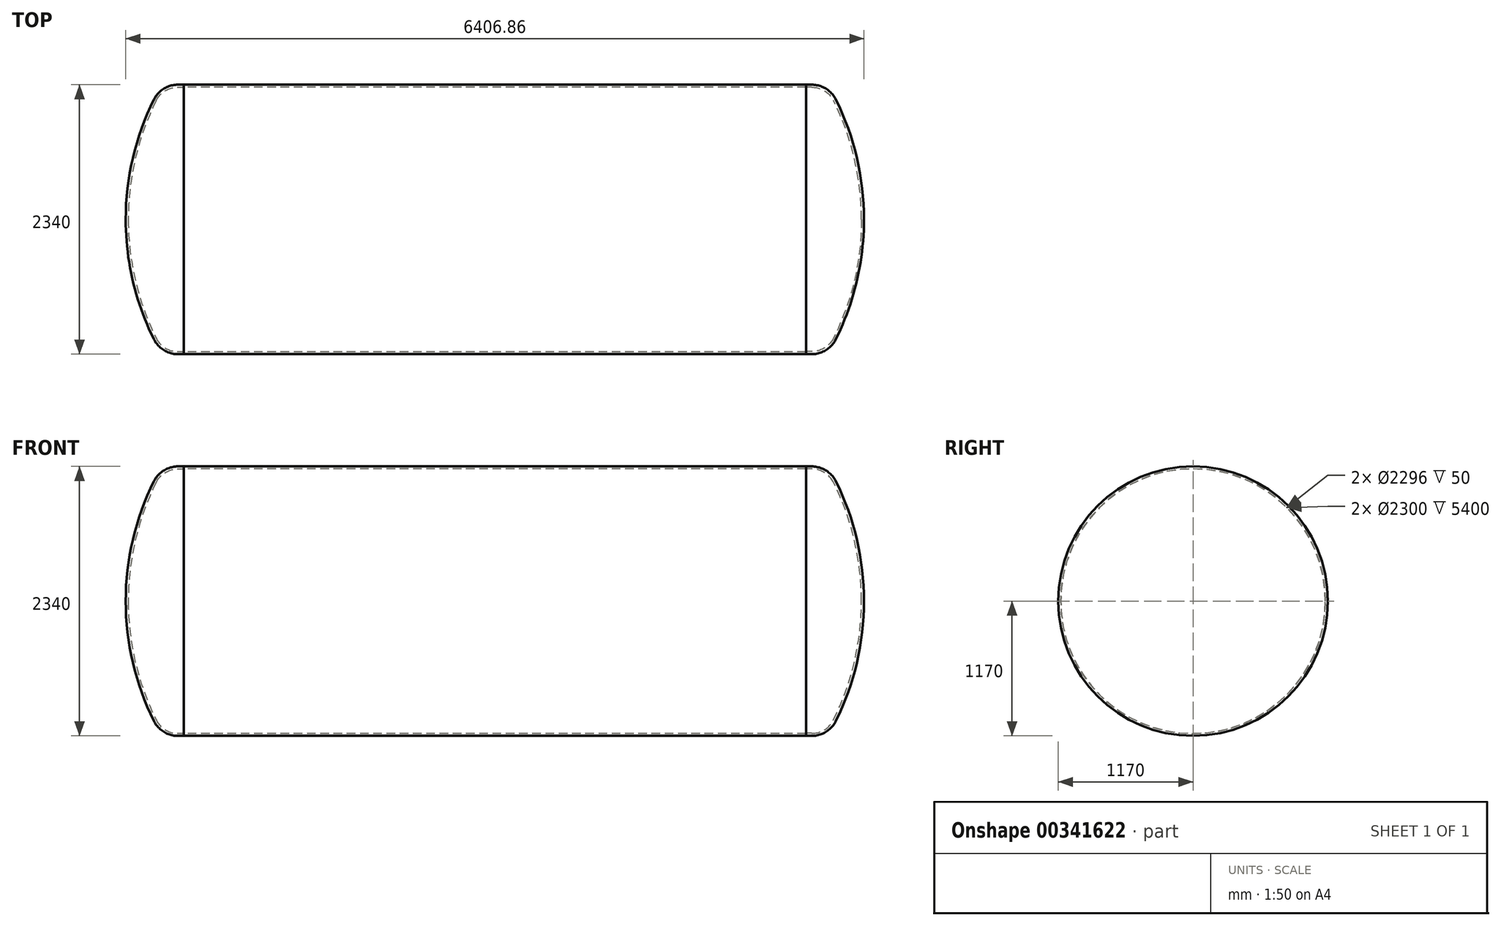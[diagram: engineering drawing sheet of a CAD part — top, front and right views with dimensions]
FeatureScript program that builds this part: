
annotation { "Feature Type Name" : "Feature", "Feature Type Description" : "" }
export const myFeature = defineFeature(function(context is Context, id is Id, definition is map)
    precondition{}
    {
        {
            var Q0;
            Q0=qCreatedBy(makeId("Right.planeOp"),FACE);
            var sketch = newSketch(context, id + "F0", { "sketchPlane" : qUnion([Q0])});
            skCircle(sketch, "E0", {"center": v(0, 0) * mm, "radius": 1150 * mm});
            skCircle(sketch, "E1", {"center": v(0, 0) * mm, "radius": 1170 * mm});
            skSolve(sketch);
        }
        {
            var Q0;
            Q0 = qSketchRegion(id + "F0", true);
            extrude(context, id + "F1", {"entities" : qUnion([Q0]), "oppositeDirection" : true, "depth" : 2700 * mm});
        }
        {
            var Q0;
            Q0=qCreatedBy(makeId("Top.planeOp"),FACE);
            var sketch = newSketch(context, id + "F2", { "sketchPlane" : qUnion([Q0])});
            skLineSegment(sketch, "E2", {"start": v(-5400, 1170) * mm, "end": v(0, 1170) * mm});
            skLineSegment(sketch, "E3", {"start": v(0, -1170) * mm, "end": v(50, -1170) * mm});
            skLineSegment(sketch, "E4", {"start": v(-1836.57, 0) * mm, "end": v(0, 0) * mm, "construction": true});
            skArc(sketch, "E5", {"start": v(259.62, -1040) * mm, "mid": v(441.66, -534.1) * mm, "end": v(503.43, 0) * mm});
            skArc(sketch, "E6", {"start": v(50, -1170) * mm, "mid": v(173.33, -1134.86) * mm, "end": v(259.62, -1040) * mm});
            skLineSegment(sketch, "E7", {"start": v(50, -936) * mm, "end": v(50, -1170) * mm, "construction": true});
            skLineSegment(sketch, "E8", {"start": v(0, 0) * mm, "end": v(503.43, 0) * mm, "construction": true});
            skArc(sketch, "E9.0", {"start": v(239.91, -1030.22) * mm, "mid": v(420.24, -529.08) * mm, "end": v(481.43, 0) * mm});
            skArc(sketch, "E9.1", {"start": v(50, -1148) * mm, "mid": v(161.73, -1116.17) * mm, "end": v(239.91, -1030.22) * mm});
            skLineSegment(sketch, "E9.2", {"start": v(0, -1148) * mm, "end": v(50, -1148) * mm});
            skLineSegment(sketch, "E10", {"start": v(0, -1148) * mm, "end": v(0, -1170) * mm});
            skLineSegment(sketch, "E11", {"start": v(481.43, 0) * mm, "end": v(503.43, 0) * mm});
            skSolve(sketch);
        }
        {
            var Q0;
            Q0 = qSketchRegion(id + "F2", true);
            var Q1;
            Q1=sQuery(id+"F2.wireOp",EDGE,"E8");
            revolve(context, id + "F3", {"entities" : qUnion([Q0]), "axis" : qUnion([Q1]), "revolveType" : RevolveType.FULL});
        }
        {
            var Q0;
            Q0=makeQuery(id+"F1.opExtrude","SWEPT_BODY",BODY,{"disambiguationData":[OSD([sQuery(id+"F0.wireOp",EDGE,"E0"),sQuery(id+"F0.wireOp",EDGE,"E1")])]});
            var Q1;
            Q1=qCreatedBy(makeId("Right.planeOp"),FACE);
            mirror(context, id + "F4", {"entities" : qUnion([Q0]), "mirrorPlane" : qUnion([Q1])});
        }
        {
            var Q0;
            Q0=makeQuery(id+"F4.opPattern","COPY",BODY,{"derivedFrom":makeQuery(id+"F1.opExtrude","SWEPT_BODY",BODY,{"disambiguationData":[OSD([sQuery(id+"F0.wireOp",EDGE,"E0"),sQuery(id+"F0.wireOp",EDGE,"E1")])]}),"instanceName":"1"});
            deleteBodies(context, id + "F5", {"entities" : qUnion([Q0])});
        }
        {
            var Q0;
            Q0=makeQuery(id+"F1.opExtrude","CAP_FACE",FACE,{"disambiguationData":[OSD([sQuery(id+"F0.wireOp",EDGE,"E0"),sQuery(id+"F0.wireOp",EDGE,"E1")])],"isStart":false});
            cPlane(context, id + "F6", {"entities" : qUnion([Q0]), "cplaneType" : CPlaneType.OFFSET, "offset" : 0 * mm, "width" : 150 * mm, "height" : 150 * mm});
        }
        {
            var Q0;
            Q0=makeQuery(id+"F1.opExtrude","SWEPT_BODY",BODY,{"disambiguationData":[OSD([sQuery(id+"F0.wireOp",EDGE,"E0"),sQuery(id+"F0.wireOp",EDGE,"E1")])]});
            var Q1;
            Q1=qCreatedBy(id+"F6.planeOp",FACE);
            mirror(context, id + "F7", {"operationType" : NewBodyOperationType.ADD, "entities" : qUnion([Q0]), "mirrorPlane" : qUnion([Q1])});
        }
        {
            var Q0;
            Q0=makeQuery(id+"F3.opRevolve","SWEPT_BODY",BODY,{"disambiguationData":[OSD([sQuery(id+"F2.wireOp",EDGE,"E3"),sQuery(id+"F2.wireOp",EDGE,"E5"),sQuery(id+"F2.wireOp",EDGE,"E6"),sQuery(id+"F2.wireOp",EDGE,"E9.0"),sQuery(id+"F2.wireOp",EDGE,"E9.1"),sQuery(id+"F2.wireOp",EDGE,"E9.2"),sQuery(id+"F2.wireOp",EDGE,"E10"),sQuery(id+"F2.wireOp",EDGE,"E11")])]});
            var Q1;
            Q1=qCreatedBy(id+"F6.planeOp",FACE);
            mirror(context, id + "F8", {"entities" : qUnion([Q0]), "mirrorPlane" : qUnion([Q1])});
        }
    });
